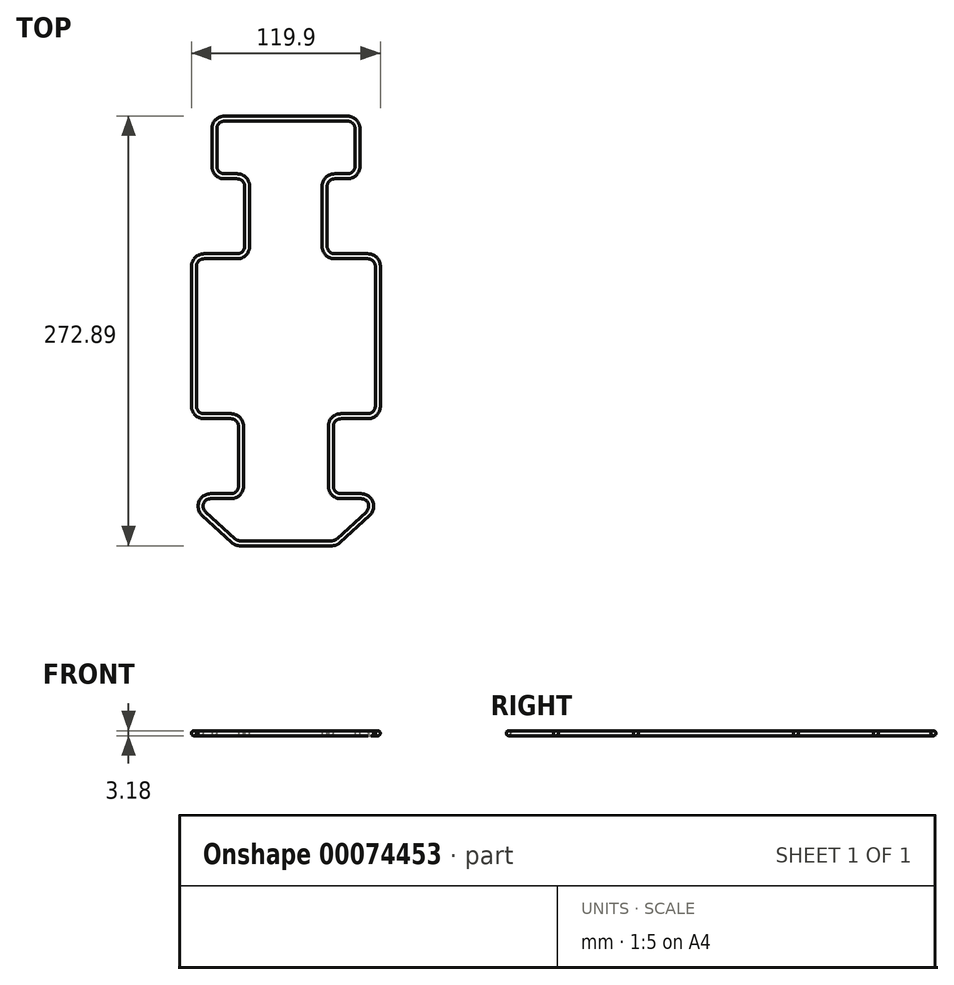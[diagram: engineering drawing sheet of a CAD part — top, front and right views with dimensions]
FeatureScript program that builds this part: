
annotation { "Feature Type Name" : "Feature", "Feature Type Description" : "" }
export const myFeature = defineFeature(function(context is Context, id is Id, definition is map)
    precondition{}
    {
        {
            var Q0;
            Q0=qCreatedBy(makeId("Top.planeOp"),FACE);
            var sketch = newSketch(context, id + "F0", { "sketchPlane" : qUnion([Q0])});
            skLineSegment(sketch, "E0", {"start": v(0, 0) * mm, "end": v(29.16, 0) * mm});
            skLineSegment(sketch, "E1", {"start": v(33.45, 1.68) * mm, "end": v(52.14, 18.86) * mm});
            skLineSegment(sketch, "E2", {"start": v(47.84, 29.89) * mm, "end": v(34.9, 29.89) * mm});
            skLineSegment(sketch, "E3", {"start": v(28.55, 36.24) * mm, "end": v(28.55, 74.34) * mm});
            skLineSegment(sketch, "E4", {"start": v(34.9, 80.69) * mm, "end": v(52.02, 80.69) * mm});
            skLineSegment(sketch, "E5", {"start": v(58.37, 87.04) * mm, "end": v(58.37, 175.94) * mm});
            skLineSegment(sketch, "E6", {"start": v(52.02, 182.29) * mm, "end": v(30.96, 182.29) * mm});
            skLineSegment(sketch, "E7", {"start": v(24.61, 188.64) * mm, "end": v(24.61, 226.74) * mm});
            skLineSegment(sketch, "E8", {"start": v(30.96, 233.09) * mm, "end": v(39.08, 233.09) * mm});
            skLineSegment(sketch, "E9", {"start": v(45.43, 239.44) * mm, "end": v(45.43, 263.36) * mm});
            skLineSegment(sketch, "E10", {"start": v(39.08, 269.71) * mm, "end": v(0, 269.71) * mm});
            skPoint(sketch, "E11.visualSharp", {"position": v(31.63, 0) * mm});
            skArc(sketch, "E11.filletArc", {"start": v(29.16, 0) * mm, "mid": v(31.46, 0.43) * mm, "end": v(33.45, 1.68) * mm});
            skPoint(sketch, "E12.visualSharp", {"position": v(64.13, 29.89) * mm});
            skArc(sketch, "E12.filletArc", {"start": v(52.14, 18.86) * mm, "mid": v(53.76, 25.85) * mm, "end": v(47.84, 29.89) * mm});
            skPoint(sketch, "E13.visualSharp", {"position": v(28.55, 29.89) * mm});
            skArc(sketch, "E13.filletArc", {"start": v(28.55, 36.24) * mm, "mid": v(30.4, 31.75) * mm, "end": v(34.9, 29.89) * mm});
            skPoint(sketch, "E14.visualSharp", {"position": v(28.55, 80.69) * mm});
            skArc(sketch, "E14.filletArc", {"start": v(34.9, 80.69) * mm, "mid": v(30.4, 78.83) * mm, "end": v(28.55, 74.34) * mm});
            skPoint(sketch, "E15.visualSharp", {"position": v(58.37, 80.69) * mm});
            skArc(sketch, "E15.filletArc", {"start": v(52.02, 80.69) * mm, "mid": v(56.5, 82.55) * mm, "end": v(58.37, 87.04) * mm});
            skPoint(sketch, "E16.visualSharp", {"position": v(58.37, 182.29) * mm});
            skArc(sketch, "E16.filletArc", {"start": v(58.37, 175.94) * mm, "mid": v(56.5, 180.43) * mm, "end": v(52.02, 182.29) * mm});
            skPoint(sketch, "E17.visualSharp", {"position": v(24.61, 182.29) * mm});
            skArc(sketch, "E17.filletArc", {"start": v(24.61, 188.64) * mm, "mid": v(26.47, 184.15) * mm, "end": v(30.96, 182.29) * mm});
            skPoint(sketch, "E18.visualSharp", {"position": v(24.61, 233.09) * mm});
            skArc(sketch, "E18.filletArc", {"start": v(30.96, 233.09) * mm, "mid": v(26.47, 231.23) * mm, "end": v(24.61, 226.74) * mm});
            skPoint(sketch, "E19.visualSharp", {"position": v(45.43, 233.09) * mm});
            skArc(sketch, "E19.filletArc", {"start": v(39.08, 233.09) * mm, "mid": v(43.57, 234.95) * mm, "end": v(45.43, 239.44) * mm});
            skPoint(sketch, "E20.visualSharp", {"position": v(45.43, 269.71) * mm});
            skArc(sketch, "E20.filletArc", {"start": v(45.43, 263.36) * mm, "mid": v(43.57, 267.85) * mm, "end": v(39.08, 269.71) * mm});
            skSolve(sketch);
        }
        {
            var Q0;
            Q0=qCreatedBy(makeId("Right.planeOp"),FACE);
            var sketch = newSketch(context, id + "F1", { "sketchPlane" : qUnion([Q0])});
            skCircle(sketch, "E21", {"center": v(0, 0) * mm, "radius": 1.59 * mm});
            skSolve(sketch);
        }
        {
            var Q0;
            Q0=makeQuery(id+"F1.imprint","IMPRINT",FACE,{"disambiguationData":[TD([[makeQuery(id+"F1.imprint","IMPRINT",EDGE,{"derivedFrom":sQuery(id+"F1.wireOp",EDGE,"E21")}),1.0]])]});
            var Q1;
            Q1 = qConstructionFilter(qBodyType(qCreatedBy(id + "F0" ,EDGE), BodyType.WIRE), ConstructionObject.NO);
            sweep(context, id + "F2", {"profiles" : qUnion([Q0]), "path" : qUnion([Q1])});
        }
        {
            var Q0;
            Q0=makeQuery(id+"F2.opSweep","SWEPT_BODY",BODY,{"disambiguationData":[OSD([sQuery(id+"F0.wireOp",EDGE,"E5"),sQuery(id+"F1.wireOp",EDGE,"E21")])]});
            var Q1;
            Q1=qCreatedBy(makeId("Right.planeOp"),FACE);
            mirror(context, id + "F3", {"operationType" : NewBodyOperationType.ADD, "entities" : qUnion([Q0]), "mirrorPlane" : qUnion([Q1])});
        }
    });
